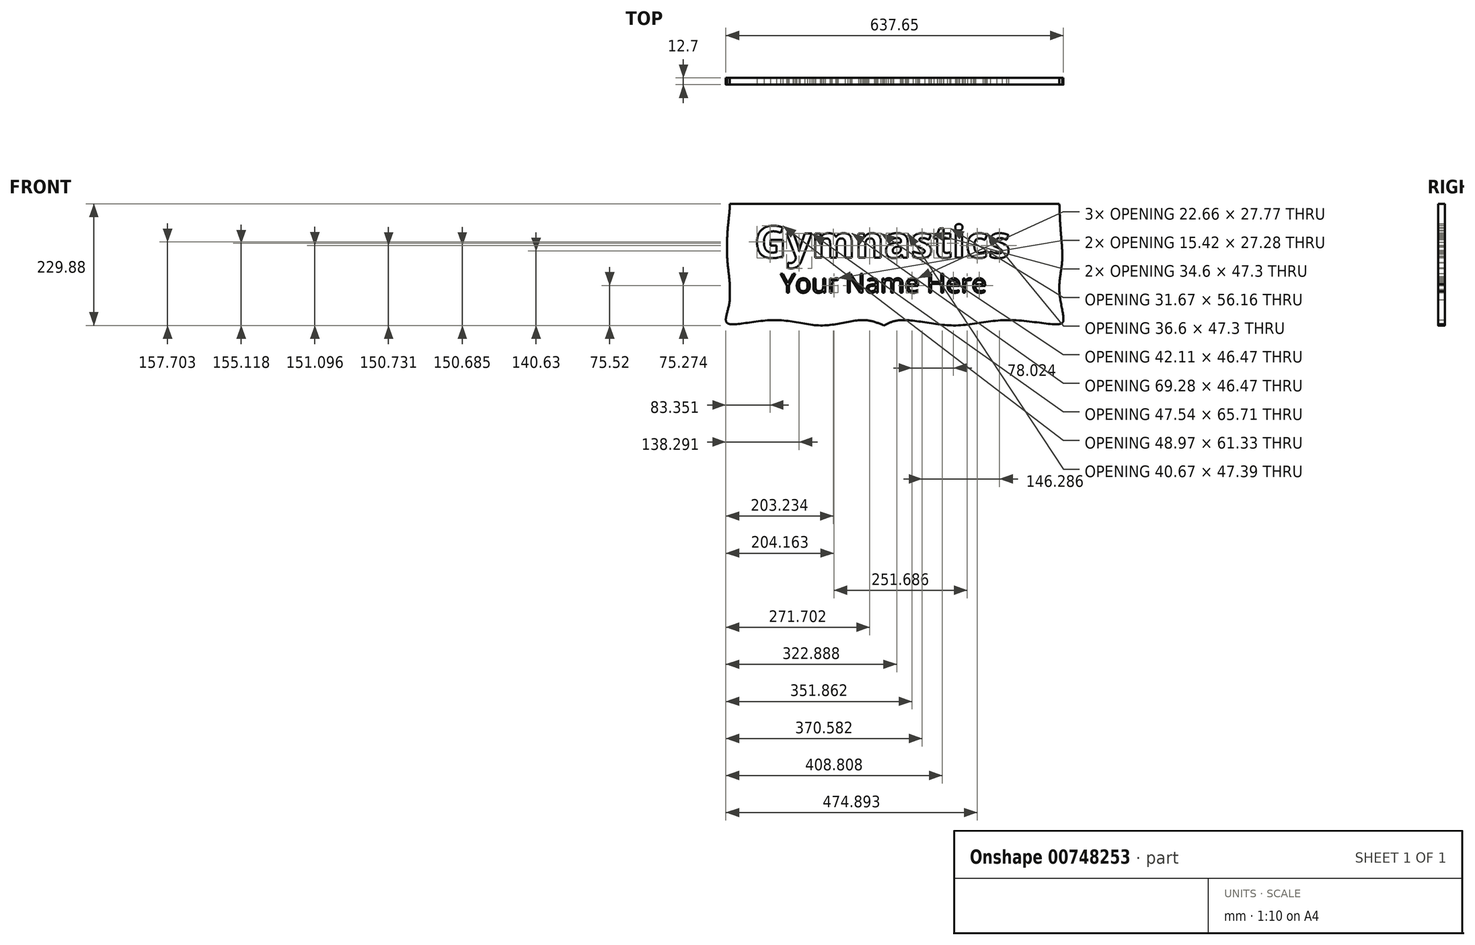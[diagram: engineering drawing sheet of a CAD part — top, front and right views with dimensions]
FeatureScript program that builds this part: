
annotation { "Feature Type Name" : "Feature", "Feature Type Description" : "" }
export const myFeature = defineFeature(function(context is Context, id is Id, definition is map)
    precondition{}
    {
        {
            var Q0;
            Q0=qCreatedBy(makeId("Front.planeOp"),FACE);
            var sketch = newSketch(context, id + "F0", { "sketchPlane" : qUnion([Q0])});
            skLineSegment(sketch, "E0.bottom", {"start": v(-290.57, 105.94) * mm, "end": v(331.73, 105.94) * mm});
            skLineSegment(sketch, "E0.top", {"start": v(-290.57, -113.77) * mm, "end": v(331.73, -113.77) * mm});
            skLineSegment(sketch, "E0.left", {"start": v(-290.57, 105.94) * mm, "end": v(-290.57, -113.77) * mm});
            skLineSegment(sketch, "E0.right", {"start": v(331.73, 105.94) * mm, "end": v(331.73, -113.77) * mm});
            skSolve(sketch);
        }
        {
            var Q0;
            Q0=makeQuery(id+"F0.imprint","IMPRINT",FACE,{"disambiguationData":[TD([[makeQuery(id+"F0.imprint","IMPRINT",EDGE,{"derivedFrom":sQuery(id+"F0.wireOp",EDGE,"E0.bottom")}),-1.0]])]});
            extrude(context, id + "F1", {"entities" : qUnion([Q0]), "depth" : 12.7 * mm, "offsetDistance" : 25.4 * mm});
        }
        {
            var Q0;
            Q0=makeQuery(id+"F1.opExtrude","CAP_FACE",FACE,{"disambiguationData":[OSD([sQuery(id+"F0.wireOp",EDGE,"E0.bottom"),sQuery(id+"F0.wireOp",EDGE,"E0.top"),sQuery(id+"F0.wireOp",EDGE,"E0.left"),sQuery(id+"F0.wireOp",EDGE,"E0.right")])],"isStart":false});
            var sketch = newSketch(context, id + "F2", { "sketchPlane" : qUnion([Q0])});
            skText(sketch, "E1", { "text": "Gymnastics", "fontName": "OpenSans-Bold.ttf"});
            const initialGuessF2  = {"E1": [-0.24421, 0.00392, 1, 0, 0.06017]};
            skSetInitialGuess(sketch, initialGuessF2);
            skSolve(sketch);
        }
        {
            var Q0;
            Q0=makeQuery(id+"F2.imprint","IMPRINT",FACE,{"disambiguationData":[TD([[makeQuery(id+"F2.imprint","IMPRINT",EDGE,{"derivedFrom":sQuery(id+"F2.wireOp",EDGE,"E1.sketch_text.stroke-0")}),1.0]])]});
            var sketch = newSketch(context, id + "F3", { "sketchPlane" : qUnion([Q0])});
            skText(sketch, "E2", { "text": "Your Name Here", "fontName": "OpenSans-Regular.ttf"});
            const initialGuessF3  = {"E2": [-0.19506, -0.06206, 1, 0, 0.03604]};
            skSetInitialGuess(sketch, initialGuessF3);
            skSolve(sketch);
        }
        {
            var Q0;
            Q0=qSketchRegion(id+"F2",true);
            var Q1;
            Q1=qSketchRegion(id+"F3",true);
            extrude(context, id + "F4", {"entities" : qUnion([Q0, Q1]), "operationType" : NewBodyOperationType.REMOVE, "oppositeDirection" : true, "depth" : 25.4 * mm, "offsetDistance" : 25.4 * mm});
        }
        {
            var Q0;
            {var subQ0=sQuery(id+"F0.wireOp",EDGE,"E0.right");var subQ1=sQuery(id+"F0.wireOp",EDGE,"E0.bottom");var subQ2=sQuery(id+"F0.wireOp",EDGE,"E0.left");var subQ3=sQuery(id+"F0.wireOp",EDGE,"E0.top");Q0=makeQuery(id+"F4.boolean.opBoolean","SPLIT",FACE,{"disambiguationData":[TD([makeQuery(id+"F1.opExtrude","SWEPT_FACE",FACE,{"disambiguationData":[OSD([subQ1])]})])],"derivedFrom":makeQuery(id+"F1.opExtrude","CAP_FACE",FACE,{"disambiguationData":[OSD([subQ1,subQ3,subQ2,subQ0])],"isStart":false})});}
            var sketch = newSketch(context, id + "F5", { "sketchPlane" : qUnion([Q0])});
            skPoint(sketch, "E3", {"position": v(-290.57, -75.67) * mm});
            skPoint(sketch, "E4", {"position": v(-290.57, 4.34) * mm});
            skPoint(sketch, "E5", {"position": v(-290.57, 74.2) * mm});
            skLineSegment(sketch, "E6", {"start": v(-290.57, 74.2) * mm, "end": v(-293.1, 74.2) * mm});
            skLineSegment(sketch, "E7", {"start": v(-290.57, 4.34) * mm, "end": v(-295.65, 4.34) * mm});
            skLineSegment(sketch, "E8", {"start": v(-290.57, -113.77) * mm, "end": v(-298.19, -113.77) * mm});
            skLineSegment(sketch, "E9", {"start": v(-290.57, -113.77) * mm, "end": v(-290.57, -121.39) * mm});
            skPoint(sketch, "E10", {"position": v(-210.29, -113.77) * mm});
            skPoint(sketch, "E11", {"position": v(0, -113.77) * mm});
            skPoint(sketch, "E12", {"position": v(-39.3, -113.77) * mm});
            skPoint(sketch, "E13", {"position": v(-115.36, -113.77) * mm});
            skPoint(sketch, "E14", {"position": v(33.42, -113.77) * mm});
            skPoint(sketch, "E15", {"position": v(131.68, -113.77) * mm});
            skPoint(sketch, "E16", {"position": v(235.49, -113.77) * mm});
            skPoint(sketch, "E17", {"position": v(331.73, -59.7) * mm});
            skPoint(sketch, "E18", {"position": v(331.73, -3.91) * mm});
            skPoint(sketch, "E19", {"position": v(331.73, 54.1) * mm});
            skLineSegment(sketch, "E20", {"start": v(331.73, 54.1) * mm, "end": v(334.27, 54.1) * mm});
            skLineSegment(sketch, "E21", {"start": v(331.73, -3.91) * mm, "end": v(336.81, -3.91) * mm});
            skLineSegment(sketch, "E22", {"start": v(331.73, -113.77) * mm, "end": v(339.35, -113.77) * mm});
            skLineSegment(sketch, "E23", {"start": v(331.73, -113.77) * mm, "end": v(331.73, -121.39) * mm});
            skLineSegment(sketch, "E24", {"start": v(-115.36, -113.77) * mm, "end": v(-115.36, -123.93) * mm});
            skLineSegment(sketch, "E25", {"start": v(0, -113.77) * mm, "end": v(0, -123.93) * mm});
            skLineSegment(sketch, "E26", {"start": v(131.68, -113.77) * mm, "end": v(131.68, -123.93) * mm});
            skFitSpline(sketch, "E27", {"points": [v(-290.57, 105.94) * mm, v(-293.1, 74.2) * mm, v(-295.65, 4.34) * mm, v(-290.57, -75.67) * mm, v(-298.19, -113.77) * mm, v(-290.57, -121.39) * mm, v(-206.79, -113.77) * mm, v(-115.36, -123.93) * mm, v(-39.3, -113.77) * mm, v(0, -123.93) * mm], "startDerivative": vector(-16.13, -484.78) * mm, "endDerivative": vector(374.15, -159.82) * mm});
            skFitSpline(sketch, "E28", {"points": [v(331.73, 105.94) * mm, v(334.27, 54.1) * mm, v(336.81, -3.91) * mm, v(331.73, -59.7) * mm, v(339.35, -113.77) * mm, v(331.73, -121.39) * mm, v(235.49, -113.77) * mm, v(131.68, -123.93) * mm, v(33.42, -113.77) * mm, v(0, -123.93) * mm], "startDerivative": vector(15.9, -475.63) * mm, "endDerivative": vector(-324.26, -164.08) * mm});
            skSolve(sketch);
        }
        {
            var Q0;
            {var subQ0=sQuery(id+"F5.wireOp",EDGE,"E25");Q0=makeQuery(id+"F5.imprint","IMPRINT",FACE,{"disambiguationData":[TD([[makeQuery(id+"F5.imprint","IMPRINT",EDGE,{"derivedFrom":subQ0}),-1.0]])]});}
            var Q1;
            {var subQ0=sQuery(id+"F5.wireOp",EDGE,"E25");Q1=makeQuery(id+"F5.imprint","IMPRINT",FACE,{"disambiguationData":[TD([[makeQuery(id+"F5.imprint","IMPRINT",EDGE,{"derivedFrom":subQ0}),1.0]])]});}
            var Q2;
            {var subQ0=sQuery(id+"F5.wireOp",EDGE,"E24");Q2=makeQuery(id+"F5.imprint","IMPRINT",FACE,{"disambiguationData":[TD([[makeQuery(id+"F5.imprint","IMPRINT",EDGE,{"derivedFrom":subQ0}),1.0]])]});}
            var Q3;
            {var subQ0=sQuery(id+"F5.wireOp",EDGE,"E24");Q3=makeQuery(id+"F5.imprint","IMPRINT",FACE,{"disambiguationData":[TD([[makeQuery(id+"F5.imprint","IMPRINT",EDGE,{"derivedFrom":subQ0}),-1.0]])]});}
            var Q4;
            {var subQ0=sQuery(id+"F5.wireOp",EDGE,"E9");Q4=makeQuery(id+"F5.imprint","IMPRINT",FACE,{"disambiguationData":[TD([[makeQuery(id+"F5.imprint","IMPRINT",EDGE,{"derivedFrom":subQ0}),1.0]])]});}
            var Q5;
            {var subQ0=sQuery(id+"F5.wireOp",EDGE,"E8");Q5=makeQuery(id+"F5.imprint","IMPRINT",FACE,{"disambiguationData":[TD([[makeQuery(id+"F5.imprint","IMPRINT",EDGE,{"derivedFrom":subQ0}),1.0]])]});}
            var Q6;
            {var subQ0=sQuery(id+"F5.wireOp",EDGE,"E8");Q6=makeQuery(id+"F5.imprint","IMPRINT",FACE,{"disambiguationData":[TD([[makeQuery(id+"F5.imprint","IMPRINT",EDGE,{"derivedFrom":subQ0}),-1.0]])]});}
            var Q7;
            {var subQ0=sQuery(id+"F5.wireOp",EDGE,"E7");Q7=makeQuery(id+"F5.imprint","IMPRINT",FACE,{"disambiguationData":[TD([[makeQuery(id+"F5.imprint","IMPRINT",EDGE,{"derivedFrom":subQ0}),1.0]])]});}
            var Q8;
            {var subQ0=sQuery(id+"F5.wireOp",EDGE,"E6");Q8=makeQuery(id+"F5.imprint","IMPRINT",FACE,{"disambiguationData":[TD([[makeQuery(id+"F5.imprint","IMPRINT",EDGE,{"derivedFrom":subQ0}),1.0]])]});}
            var Q9;
            {var subQ0=makeQuery(id+"F1.opExtrude","CAP_EDGE",EDGE,{"disambiguationData":[OSD([sQuery(id+"F0.wireOp",EDGE,"E0.bottom")])],"isStart":false});Q9=makeQuery(id+"F5.imprint","IMPRINT",FACE,{"disambiguationData":[TD([[makeQuery(id+"F5.imprint","IMPRINT",EDGE,{"derivedFrom":subQ0}),-1.0]])]});}
            var Q10;
            {var subQ0=sQuery(id+"F5.wireOp",EDGE,"E26");Q10=makeQuery(id+"F5.imprint","IMPRINT",FACE,{"disambiguationData":[TD([[makeQuery(id+"F5.imprint","IMPRINT",EDGE,{"derivedFrom":subQ0}),-1.0]])]});}
            var Q11;
            {var subQ0=sQuery(id+"F5.wireOp",EDGE,"E26");Q11=makeQuery(id+"F5.imprint","IMPRINT",FACE,{"disambiguationData":[TD([[makeQuery(id+"F5.imprint","IMPRINT",EDGE,{"derivedFrom":subQ0}),1.0]])]});}
            var Q12;
            {var subQ0=sQuery(id+"F5.wireOp",EDGE,"E23");Q12=makeQuery(id+"F5.imprint","IMPRINT",FACE,{"disambiguationData":[TD([[makeQuery(id+"F5.imprint","IMPRINT",EDGE,{"derivedFrom":subQ0}),-1.0]])]});}
            var Q13;
            {var subQ0=sQuery(id+"F5.wireOp",EDGE,"E22");Q13=makeQuery(id+"F5.imprint","IMPRINT",FACE,{"disambiguationData":[TD([[makeQuery(id+"F5.imprint","IMPRINT",EDGE,{"derivedFrom":subQ0}),-1.0]])]});}
            var Q14;
            {var subQ0=sQuery(id+"F5.wireOp",EDGE,"E22");Q14=makeQuery(id+"F5.imprint","IMPRINT",FACE,{"disambiguationData":[TD([[makeQuery(id+"F5.imprint","IMPRINT",EDGE,{"derivedFrom":subQ0}),1.0]])]});}
            var Q15;
            {var subQ0=sQuery(id+"F5.wireOp",EDGE,"E21");Q15=makeQuery(id+"F5.imprint","IMPRINT",FACE,{"disambiguationData":[TD([[makeQuery(id+"F5.imprint","IMPRINT",EDGE,{"derivedFrom":subQ0}),-1.0]])]});}
            var Q16;
            {var subQ0=sQuery(id+"F5.wireOp",EDGE,"E20");Q16=makeQuery(id+"F5.imprint","IMPRINT",FACE,{"disambiguationData":[TD([[makeQuery(id+"F5.imprint","IMPRINT",EDGE,{"derivedFrom":subQ0}),-1.0]])]});}
            var Q17;
            {var subQ0=sQuery(id+"F5.wireOp",EDGE,"E20");Q17=makeQuery(id+"F5.imprint","IMPRINT",FACE,{"disambiguationData":[TD([[makeQuery(id+"F5.imprint","IMPRINT",EDGE,{"derivedFrom":subQ0}),1.0]])]});}
            var Q18;
            {var subQ0=sQuery(id+"F5.wireOp",EDGE,"E6");Q18=makeQuery(id+"F5.imprint","IMPRINT",FACE,{"disambiguationData":[TD([[makeQuery(id+"F5.imprint","IMPRINT",EDGE,{"derivedFrom":subQ0}),-1.0]])]});}
            extrude(context, id + "F6", {"entities" : qUnion([Q0, Q1, Q2, Q3, Q4, Q5, Q6, Q7, Q8, Q9, Q10, Q11, Q12, Q13, Q14, Q15, Q16, Q17, Q18]), "operationType" : NewBodyOperationType.ADD, "depth" : -12.7 * mm, "offsetDistance" : 25.4 * mm});
        }
    });
